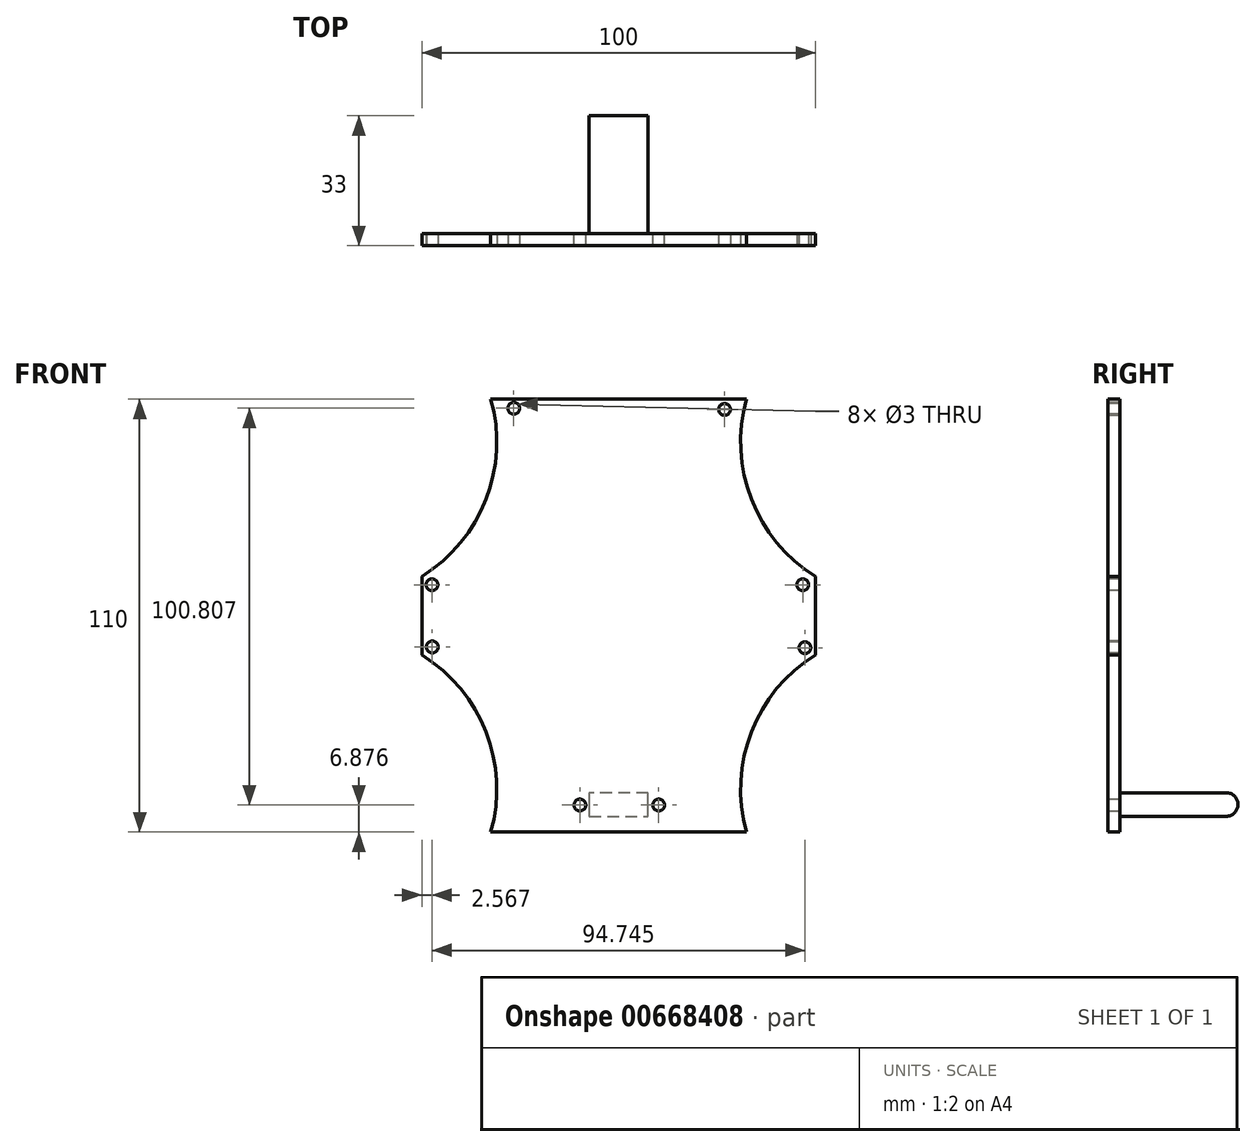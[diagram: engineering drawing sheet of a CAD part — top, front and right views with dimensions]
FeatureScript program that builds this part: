
annotation { "Feature Type Name" : "Feature", "Feature Type Description" : "" }
export const myFeature = defineFeature(function(context is Context, id is Id, definition is map)
    precondition{}
    {
        {
            var Q0;
            Q0=qCreatedBy(makeId("Front.planeOp"),FACE);
            var sketch = newSketch(context, id + "F0", { "sketchPlane" : qUnion([Q0])});
            skLineSegment(sketch, "E0.bottom", {"start": v(0, 0) * mm, "end": v(100, 0) * mm});
            skLineSegment(sketch, "E0.top", {"start": v(0, 110) * mm, "end": v(100, 110) * mm});
            skLineSegment(sketch, "E0.left", {"start": v(0, 0) * mm, "end": v(0, 110) * mm});
            skLineSegment(sketch, "E0.right", {"start": v(100, 0) * mm, "end": v(100, 110) * mm});
            skSolve(sketch);
        }
        {
            var Q0;
            Q0=makeQuery(id+"F0.imprint","IMPRINT",FACE,{"disambiguationData":[TD([[makeQuery(id+"F0.imprint","IMPRINT",EDGE,{"derivedFrom":sQuery(id+"F0.wireOp",EDGE,"E0.bottom")}),1.0]])]});
            extrude(context, id + "F1", {"entities" : qUnion([Q0]), "depth" : 3 * mm, "offsetDistance" : 25 * mm});
        }
        {
            var Q0;
            Q0=makeQuery(id+"F1.opExtrude","CAP_FACE",FACE,{"disambiguationData":[OSD([sQuery(id+"F0.wireOp",EDGE,"E0.bottom"),sQuery(id+"F0.wireOp",EDGE,"E0.top"),sQuery(id+"F0.wireOp",EDGE,"E0.left"),sQuery(id+"F0.wireOp",EDGE,"E0.right")])],"isStart":false});
            var sketch = newSketch(context, id + "F2", { "sketchPlane" : qUnion([Q0])});
            skLineSegment(sketch, "E1", {"start": v(0, 0) * mm, "end": v(0, 45) * mm});
            skLineSegment(sketch, "E2", {"start": v(0, 110) * mm, "end": v(0, 65) * mm});
            skLineSegment(sketch, "E3", {"start": v(100, 110) * mm, "end": v(100, 65) * mm});
            skLineSegment(sketch, "E4", {"start": v(100, 0) * mm, "end": v(100, 45) * mm});
            skLineSegment(sketch, "E5", {"start": v(0, 0) * mm, "end": v(17.5, 0) * mm});
            skLineSegment(sketch, "E6", {"start": v(100, 0) * mm, "end": v(82.5, 0) * mm});
            skLineSegment(sketch, "E7", {"start": v(0, 110) * mm, "end": v(17.5, 110) * mm});
            skLineSegment(sketch, "E8", {"start": v(100, 110) * mm, "end": v(82.5, 110) * mm});
            skArc(sketch, "E9", {"start": v(0, 65) * mm, "mid": v(16.3, 84.56) * mm, "end": v(17.5, 110) * mm});
            skArc(sketch, "E10", {"start": v(82.5, 110) * mm, "mid": v(83.7, 84.56) * mm, "end": v(100, 65) * mm});
            skArc(sketch, "E11", {"start": v(100, 45) * mm, "mid": v(83.7, 25.44) * mm, "end": v(82.5, 0) * mm});
            skArc(sketch, "E12", {"start": v(17.5, 0) * mm, "mid": v(16.3, 25.44) * mm, "end": v(0, 45) * mm});
            skSolve(sketch);
        }
        {
            var Q0;
            Q0=makeQuery(id+"F2.imprint","IMPRINT",FACE,{"disambiguationData":[TD([[makeQuery(id+"F2.imprint","IMPRINT",EDGE,{"derivedFrom":sQuery(id+"F2.wireOp",EDGE,"E2")}),-1.0]])]});
            var Q1;
            Q1=makeQuery(id+"F2.imprint","IMPRINT",FACE,{"disambiguationData":[TD([[makeQuery(id+"F2.imprint","IMPRINT",EDGE,{"derivedFrom":sQuery(id+"F2.wireOp",EDGE,"E3")}),1.0]])]});
            var Q2;
            Q2=makeQuery(id+"F2.imprint","IMPRINT",FACE,{"disambiguationData":[TD([[makeQuery(id+"F2.imprint","IMPRINT",EDGE,{"derivedFrom":sQuery(id+"F2.wireOp",EDGE,"E4")}),1.0]])]});
            var Q3;
            Q3=makeQuery(id+"F2.imprint","IMPRINT",FACE,{"disambiguationData":[TD([[makeQuery(id+"F2.imprint","IMPRINT",EDGE,{"derivedFrom":sQuery(id+"F2.wireOp",EDGE,"E1")}),-1.0]])]});
            extrude(context, id + "F3", {"entities" : qUnion([Q0, Q1, Q2, Q3]), "operationType" : NewBodyOperationType.REMOVE, "oppositeDirection" : true, "depth" : 25 * mm, "offsetDistance" : 25 * mm});
        }
        {
            var Q0;
            Q0=makeQuery(id+"F1.opExtrude","CAP_FACE",FACE,{"disambiguationData":[OSD([sQuery(id+"F0.wireOp",EDGE,"E0.bottom"),sQuery(id+"F0.wireOp",EDGE,"E0.top"),sQuery(id+"F0.wireOp",EDGE,"E0.left"),sQuery(id+"F0.wireOp",EDGE,"E0.right")])],"isStart":true});
            var sketch = newSketch(context, id + "F4", { "sketchPlane" : qUnion([Q0])});
            skLineSegment(sketch, "E13", {"start": v(-82.5, 0) * mm, "end": v(-57.5, 0) * mm});
            skLineSegment(sketch, "E14", {"start": v(-17.5, 0) * mm, "end": v(-42.5, 0) * mm});
            skLineSegment(sketch, "E15", {"start": v(-42.5, 4) * mm, "end": v(-57.5, 4) * mm});
            skLineSegment(sketch, "E16", {"start": v(-57.5, 4) * mm, "end": v(-57.5, 10) * mm});
            skLineSegment(sketch, "E17", {"start": v(-57.5, 10) * mm, "end": v(-42.5, 10) * mm});
            skLineSegment(sketch, "E18", {"start": v(-42.5, 10) * mm, "end": v(-42.5, 4) * mm});
            skSolve(sketch);
        }
        {
            var Q0;
            Q0=makeQuery(id+"F4.imprint","IMPRINT",FACE,{"disambiguationData":[TD([[makeQuery(id+"F4.imprint","IMPRINT",EDGE,{"derivedFrom":sQuery(id+"F4.wireOp",EDGE,"E15")}),-1.0]])]});
            extrude(context, id + "F5", {"entities" : qUnion([Q0]), "operationType" : NewBodyOperationType.ADD, "depth" : 30 * mm, "offsetDistance" : 25 * mm});
        }
        {
            var Q0;
            Q0=makeQuery(id+"F5.opExtrude","CAP_EDGE",EDGE,{"disambiguationData":[OSD([sQuery(id+"F4.wireOp",EDGE,"E15")])],"isStart":false});
            fillet(context, id + "F6", {"entities" : qUnion([Q0]), "radius" : 3 * mm, "tangentPropagation" : true, "allowEdgeOverflow" : false});
        }
        {
            var Q0;
            Q0=makeQuery(id+"F5.opExtrude","CAP_EDGE",EDGE,{"disambiguationData":[OSD([sQuery(id+"F4.wireOp",EDGE,"E17")])],"isStart":false});
            fillet(context, id + "F7", {"entities" : qUnion([Q0]), "radius" : 3 * mm, "tangentPropagation" : true, "allowEdgeOverflow" : false});
        }
        {
            var Q0;
            Q0=makeQuery(id+"F1.opExtrude","CAP_FACE",FACE,{"disambiguationData":[OSD([sQuery(id+"F0.wireOp",EDGE,"E0.bottom"),sQuery(id+"F0.wireOp",EDGE,"E0.top"),sQuery(id+"F0.wireOp",EDGE,"E0.left"),sQuery(id+"F0.wireOp",EDGE,"E0.right")])],"isStart":true});
            var sketch = newSketch(context, id + "F8", { "sketchPlane" : qUnion([Q0])});
            skCircle(sketch, "E19", {"center": v(-40.15, 6.88) * mm, "radius": 1.5 * mm});
            skCircle(sketch, "E20", {"center": v(-60.15, 6.88) * mm, "radius": 1.5 * mm});
            skSolve(sketch);
        }
        {
            var Q0;
            Q0=makeQuery(id+"F8.imprint","IMPRINT",FACE,{"disambiguationData":[TD([[makeQuery(id+"F8.imprint","IMPRINT",EDGE,{"derivedFrom":sQuery(id+"F8.wireOp",EDGE,"E19")}),1.0]])]});
            var Q1;
            Q1=makeQuery(id+"F8.imprint","IMPRINT",FACE,{"disambiguationData":[TD([[makeQuery(id+"F8.imprint","IMPRINT",EDGE,{"derivedFrom":sQuery(id+"F8.wireOp",EDGE,"E20")}),1.0]])]});
            extrude(context, id + "F9", {"entities" : qUnion([Q0, Q1]), "operationType" : NewBodyOperationType.REMOVE, "oppositeDirection" : true, "depth" : 25 * mm, "offsetDistance" : 25 * mm});
        }
        {
            var Q0;
            Q0=makeQuery(id+"F1.opExtrude","CAP_FACE",FACE,{"disambiguationData":[OSD([sQuery(id+"F0.wireOp",EDGE,"E0.bottom"),sQuery(id+"F0.wireOp",EDGE,"E0.top"),sQuery(id+"F0.wireOp",EDGE,"E0.left"),sQuery(id+"F0.wireOp",EDGE,"E0.right")])],"isStart":false});
            var sketch = newSketch(context, id + "F10", { "sketchPlane" : qUnion([Q0])});
            skCircle(sketch, "E21", {"center": v(23.34, 107.68) * mm, "radius": 1.5 * mm});
            skCircle(sketch, "E22", {"center": v(76.88, 107.37) * mm, "radius": 1.5 * mm});
            skSolve(sketch);
        }
        {
            var Q0;
            Q0=makeQuery(id+"F10.imprint","IMPRINT",FACE,{"disambiguationData":[TD([[makeQuery(id+"F10.imprint","IMPRINT",EDGE,{"derivedFrom":sQuery(id+"F10.wireOp",EDGE,"E21")}),1.0]])]});
            var Q1;
            Q1=makeQuery(id+"F10.imprint","IMPRINT",FACE,{"disambiguationData":[TD([[makeQuery(id+"F10.imprint","IMPRINT",EDGE,{"derivedFrom":sQuery(id+"F10.wireOp",EDGE,"E22")}),1.0]])]});
            extrude(context, id + "F11", {"entities" : qUnion([Q0, Q1]), "operationType" : NewBodyOperationType.REMOVE, "oppositeDirection" : true, "depth" : 25 * mm, "offsetDistance" : 25 * mm});
        }
        {
            var Q0;
            Q0=makeQuery(id+"F1.opExtrude","CAP_FACE",FACE,{"disambiguationData":[OSD([sQuery(id+"F0.wireOp",EDGE,"E0.bottom"),sQuery(id+"F0.wireOp",EDGE,"E0.top"),sQuery(id+"F0.wireOp",EDGE,"E0.left"),sQuery(id+"F0.wireOp",EDGE,"E0.right")])],"isStart":false});
            var sketch = newSketch(context, id + "F12", { "sketchPlane" : qUnion([Q0])});
            skCircle(sketch, "E23", {"center": v(2.57, 62.84) * mm, "radius": 1.5 * mm});
            skCircle(sketch, "E24", {"center": v(96.77, 62.83) * mm, "radius": 1.5 * mm});
            skCircle(sketch, "E25", {"center": v(97.31, 46.84) * mm, "radius": 1.5 * mm});
            skCircle(sketch, "E26", {"center": v(2.76, 46.84) * mm, "radius": 1.5 * mm});
            skSolve(sketch);
        }
        {
            var Q0;
            Q0=makeQuery(id+"F12.imprint","IMPRINT",FACE,{"disambiguationData":[TD([[makeQuery(id+"F12.imprint","IMPRINT",EDGE,{"derivedFrom":sQuery(id+"F12.wireOp",EDGE,"E24")}),1.0]])]});
            var Q1;
            Q1=makeQuery(id+"F12.imprint","IMPRINT",FACE,{"disambiguationData":[TD([[makeQuery(id+"F12.imprint","IMPRINT",EDGE,{"derivedFrom":sQuery(id+"F12.wireOp",EDGE,"E25")}),1.0]])]});
            var Q2;
            Q2=makeQuery(id+"F12.imprint","IMPRINT",FACE,{"disambiguationData":[TD([[makeQuery(id+"F12.imprint","IMPRINT",EDGE,{"derivedFrom":sQuery(id+"F12.wireOp",EDGE,"E23")}),1.0]])]});
            extrude(context, id + "F13", {"entities" : qUnion([Q0, Q1, Q2]), "operationType" : NewBodyOperationType.REMOVE, "oppositeDirection" : true, "depth" : 25 * mm, "offsetDistance" : 25 * mm});
        }
        {
            var Q0;
            Q0=makeQuery(id+"F1.opExtrude","CAP_FACE",FACE,{"disambiguationData":[OSD([sQuery(id+"F0.wireOp",EDGE,"E0.bottom"),sQuery(id+"F0.wireOp",EDGE,"E0.top"),sQuery(id+"F0.wireOp",EDGE,"E0.left"),sQuery(id+"F0.wireOp",EDGE,"E0.right")])],"isStart":false});
            var sketch = newSketch(context, id + "F14", { "sketchPlane" : qUnion([Q0])});
            skCircle(sketch, "E27", {"center": v(2.64, 47.03) * mm, "radius": 1.5 * mm});
            skSolve(sketch);
        }
        {
            var Q0;
            Q0 = qSketchRegion(id + "F14", true);
            extrude(context, id + "F15", {"entities" : qUnion([Q0]), "operationType" : NewBodyOperationType.REMOVE, "oppositeDirection" : true, "depth" : 25 * mm, "offsetDistance" : 25 * mm});
        }
    });
